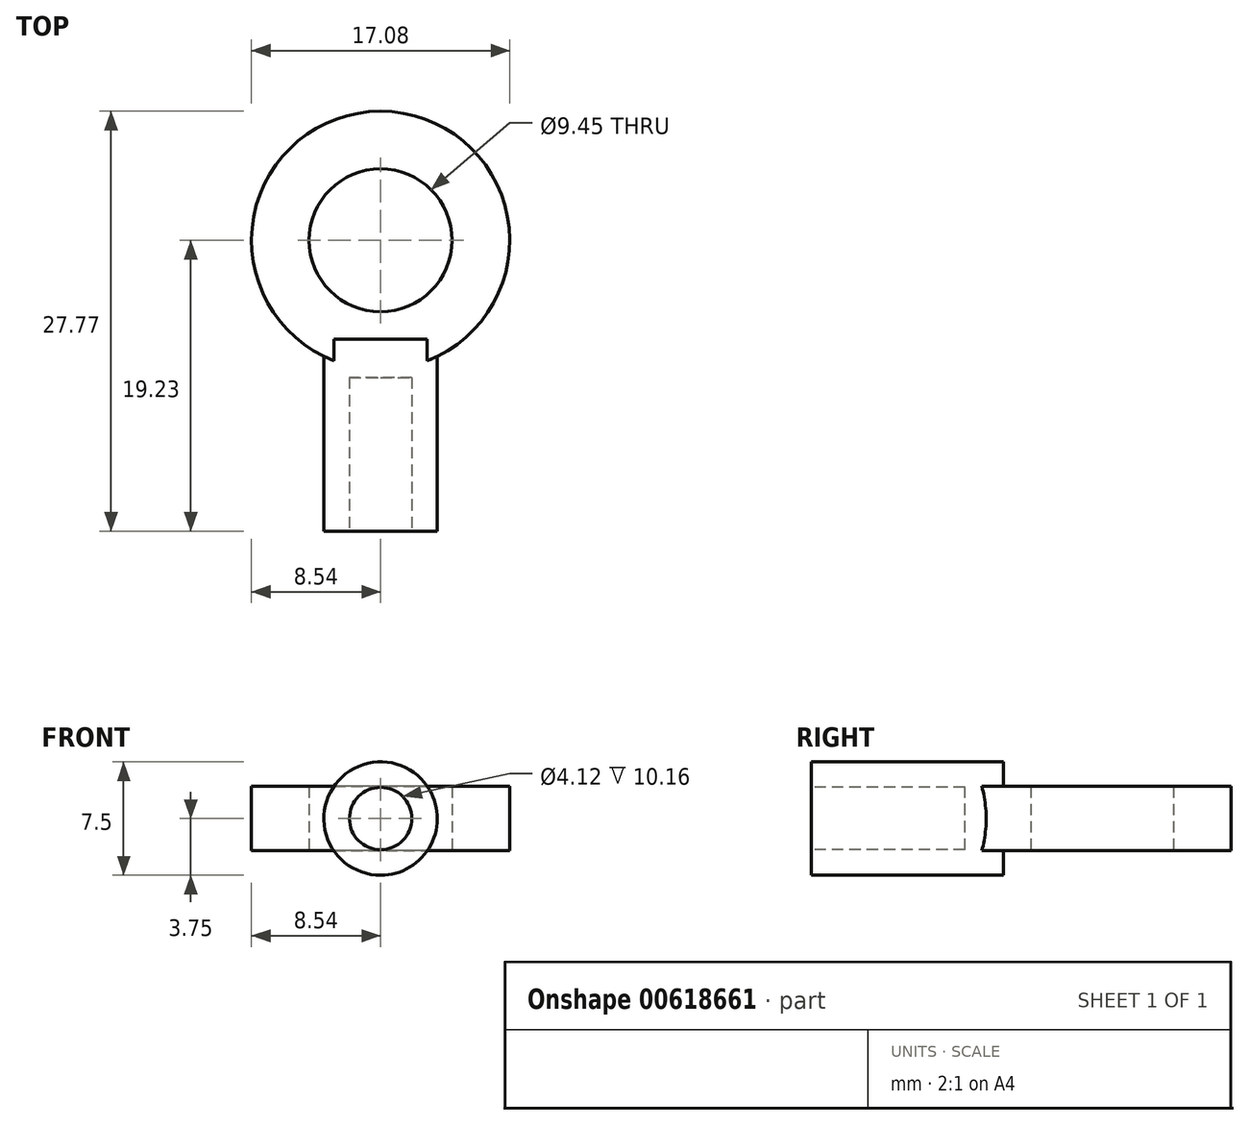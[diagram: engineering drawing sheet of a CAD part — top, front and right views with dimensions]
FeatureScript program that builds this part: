
annotation { "Feature Type Name" : "Feature", "Feature Type Description" : "" }
export const myFeature = defineFeature(function(context is Context, id is Id, definition is map)
    precondition{}
    {
        {
            var Q0;
            Q0=qCreatedBy(makeId("Top.planeOp"),FACE);
            var sketch = newSketch(context, id + "F0", { "sketchPlane" : qUnion([Q0])});
            skCircle(sketch, "E0", {"center": v(0, 0) * mm, "radius": 4.72 * mm});
            skCircle(sketch, "E1", {"center": v(0, 0) * mm, "radius": 8.54 * mm});
            skSolve(sketch);
        }
        {
            var Q0;
            Q0=qSketchRegion(id+"F0",true);
            extrude(context, id + "F1", {"entities" : qUnion([Q0]), "endBound" : BoundingType.SYMMETRIC, "depth" : 4.25 * mm, "offsetDistance" : 25.4 * mm});
        }
        {
            var Q0;
            Q0=qCreatedBy(makeId("Front.planeOp"),FACE);
            cPlane(context, id + "F2", {"entities" : qUnion([Q0]), "cplaneType" : CPlaneType.OFFSET, "offset" : (9.25 * mm / 2) + (3.8 * mm / 2), "width" : 152.4 * mm, "height" : 152.4 * mm});
        }
        {
            var Q0;
            Q0=qCreatedBy(id+"F2.planeOp",FACE);
            var sketch = newSketch(context, id + "F3", { "sketchPlane" : qUnion([Q0])});
            skCircle(sketch, "E2", {"center": v(0, 0) * mm, "radius": 3.75 * mm});
            skCircle(sketch, "E3", {"center": v(0, 0) * mm, "radius": 2 * mm});
            skSolve(sketch);
        }
        {
            var Q0;
            Q0=makeQuery(id+"F3.imprint","IMPRINT",FACE,{"disambiguationData":[TD([[makeQuery(id+"F3.imprint","IMPRINT",EDGE,{"derivedFrom":sQuery(id+"F3.wireOp",EDGE,"E3")}),1.0]])]});
            var Q1;
            Q1=makeQuery(id+"F3.imprint","IMPRINT",FACE,{"disambiguationData":[TD([[makeQuery(id+"F3.imprint","IMPRINT",EDGE,{"derivedFrom":sQuery(id+"F3.wireOp",EDGE,"E2")}),1.0]])]});
            extrude(context, id + "F4", {"entities" : qUnion([Q0, Q1]), "operationType" : NewBodyOperationType.ADD, "depth" : 12.7 * mm, "offsetDistance" : 25.4 * mm});
        }
        {
            var Q0;
            Q0=makeQuery(id+"F4.opExtrude","CAP_FACE",FACE,{"disambiguationData":[OSD([sQuery(id+"F3.wireOp",EDGE,"E2")])],"isStart":false});
            var sketch = newSketch(context, id + "F5", { "sketchPlane" : qUnion([Q0])});
            skCircle(sketch, "E4.0.0", {"center": v(0, 0) * mm, "radius": 3.75 * mm, "construction": true});
            skCircle(sketch, "E5", {"center": v(0, 0) * mm, "radius": 2.06 * mm});
            skSolve(sketch);
        }
        {
            var Q0;
            Q0=qSketchRegion(id+"F5",true);
            extrude(context, id + "F6", {"entities" : qUnion([Q0]), "operationType" : NewBodyOperationType.REMOVE, "oppositeDirection" : true, "depth" : 10.16 * mm, "offsetDistance" : 25.4 * mm});
        }
    });
